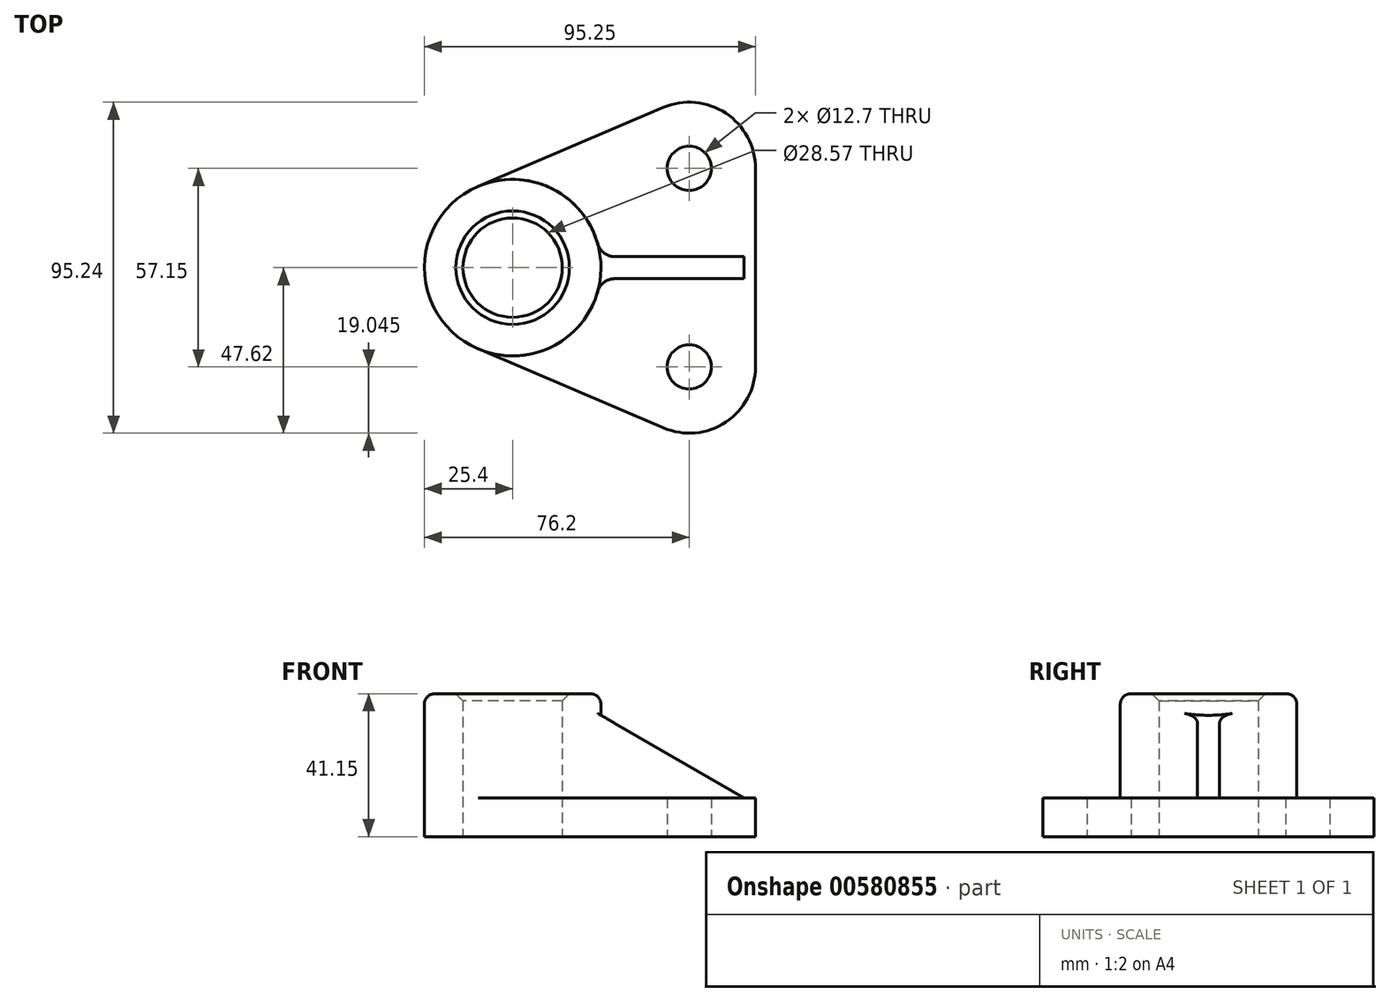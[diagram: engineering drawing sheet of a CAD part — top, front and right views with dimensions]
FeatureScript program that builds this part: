
annotation { "Feature Type Name" : "Feature", "Feature Type Description" : "" }
export const myFeature = defineFeature(function(context is Context, id is Id, definition is map)
    precondition{}
    {
        {
            var Q0;
            Q0=qCreatedBy(makeId("Top.planeOp"),FACE);
            var sketch = newSketch(context, id + "F0", { "sketchPlane" : qUnion([Q0])});
            skLineSegment(sketch, "E0", {"start": v(-101.4, 0) * mm, "end": v(116.06, 0) * mm, "construction": true});
            skCircle(sketch, "E1", {"center": v(0, 0) * mm, "radius": 14.29 * mm});
            skCircle(sketch, "E2", {"center": v(0, 0) * mm, "radius": 25.4 * mm});
            skCircle(sketch, "E3", {"center": v(50.8, -28.58) * mm, "radius": 6.35 * mm});
            skArc(sketch, "E4", {"start": v(43.33, -46.1) * mm, "mid": v(61.3, -44.47) * mm, "end": v(69.85, -28.57) * mm});
            skCircle(sketch, "E5", {"center": v(50.8, 28.58) * mm, "radius": 6.35 * mm});
            skArc(sketch, "E6", {"start": v(69.85, 28.58) * mm, "mid": v(61.3, 44.47) * mm, "end": v(43.33, 46.1) * mm});
            skLineSegment(sketch, "E7", {"start": v(69.85, 28.58) * mm, "end": v(69.85, -28.57) * mm});
            skLineSegment(sketch, "E8", {"start": v(-9.97, 23.36) * mm, "end": v(43.33, 46.1) * mm});
            skLineSegment(sketch, "E9", {"start": v(-9.97, -23.36) * mm, "end": v(43.33, -46.1) * mm});
            skSolve(sketch);
        }
        {
            var Q0;
            Q0=makeQuery(id+"F0.imprint","IMPRINT",FACE,{"disambiguationData":[TD([[makeQuery(id+"F0.imprint","IMPRINT",EDGE,{"derivedFrom":sQuery(id+"F0.wireOp",EDGE,"E1")}),-1.0]])]});
            extrude(context, id + "F1", {"entities" : qUnion([Q0]), "depth" : 41.15 * mm, "offsetDistance" : 25.4 * mm});
        }
        {
            var Q0;
            Q0=makeQuery(id+"F0.imprint","IMPRINT",FACE,{"disambiguationData":[TD([[makeQuery(id+"F0.imprint","IMPRINT",EDGE,{"derivedFrom":sQuery(id+"F0.wireOp",EDGE,"E3")}),-1.0]])]});
            extrude(context, id + "F2", {"entities" : qUnion([Q0]), "operationType" : NewBodyOperationType.ADD, "depth" : 11.18 * mm, "offsetDistance" : 25.4 * mm});
        }
        {
            var Q0;
            Q0=qCreatedBy(makeId("Front.planeOp"),FACE);
            var sketch = newSketch(context, id + "F3", { "sketchPlane" : qUnion([Q0])});
            skLineSegment(sketch, "E10", {"start": v(22.1, 36.84) * mm, "end": v(22.1, 11.18) * mm});
            skLineSegment(sketch, "E11", {"start": v(22.1, 11.18) * mm, "end": v(66.55, 11.18) * mm});
            skLineSegment(sketch, "E12", {"start": v(66.55, 11.18) * mm, "end": v(22.1, 36.84) * mm});
            skSolve(sketch);
        }
        {
            var Q0;
            Q0=makeQuery(id+"F3.imprint","IMPRINT",FACE,{"disambiguationData":[TD([[makeQuery(id+"F3.imprint","IMPRINT",EDGE,{"derivedFrom":sQuery(id+"F3.wireOp",EDGE,"E10")}),1.0]])]});
            extrude(context, id + "F4", {"entities" : qUnion([Q0]), "operationType" : NewBodyOperationType.ADD, "depth" : 6.35 * mm, "offsetDistance" : 25.4 * mm, "symmetric" : true});
        }
        {
            var Q0;
            Q0=makeQuery(id+"F1.opExtrude","CAP_EDGE",EDGE,{"disambiguationData":[OSD([sQuery(id+"F0.wireOp",EDGE,"E2")])],"isStart":false});
            fillet(context, id + "F5", {"entities" : qUnion([Q0]), "radius" : 3.05 * mm, "tangentPropagation" : true, "allowEdgeOverflow" : false});
        }
        {
            var Q0;
            Q0=makeQuery(id+"F4.opExtrude","CAP_EDGE",EDGE,{"disambiguationData":[OSD([sQuery(id+"F3.wireOp",EDGE,"E11")])],"isStart":true});
            var Q1;
            Q1=makeQuery(id+"F4.opExtrude","CAP_EDGE",EDGE,{"disambiguationData":[OSD([sQuery(id+"F3.wireOp",EDGE,"E11")])],"isStart":false});
            var Q2;
            {var subQ0=sQuery(id+"F0.wireOp",EDGE,"E2");var subQ1=sQuery(id+"F0.wireOp",EDGE,"E8");Q2=makeQuery(id+"F4.boolean.opBoolean","SPLIT",EDGE,{"disambiguationData":[TD([makeQuery(id+"F2.opExtrude","SWEPT_FACE",FACE,{"disambiguationData":[OSD([subQ1])]})])],"derivedFrom":makeQuery(id+"F2.opExtrude","CAP_EDGE",EDGE,{"disambiguationData":[OSD([subQ0])],"isStart":false})});}
            var Q3;
            {var subQ0=sQuery(id+"F0.wireOp",EDGE,"E2");var subQ1=sQuery(id+"F0.wireOp",EDGE,"E9");Q3=makeQuery(id+"F4.boolean.opBoolean","SPLIT",EDGE,{"disambiguationData":[TD([makeQuery(id+"F2.opExtrude","SWEPT_FACE",FACE,{"disambiguationData":[OSD([subQ1])]})])],"derivedFrom":makeQuery(id+"F2.opExtrude","CAP_EDGE",EDGE,{"disambiguationData":[OSD([subQ0])],"isStart":false})});}
            var Q4;
            Q4=makeQuery(id+"F4.boolean.opBoolean","INTERSECT",EDGE,{"derivedFrom":[makeQuery(id+"F1.opExtrude","SWEPT_FACE",FACE,{"disambiguationData":[OSD([sQuery(id+"F0.wireOp",EDGE,"E2")])]}),makeQuery(id+"F4.opExtrude","CAP_FACE",FACE,{"disambiguationData":[OSD([sQuery(id+"F3.wireOp",EDGE,"E10"),sQuery(id+"F3.wireOp",EDGE,"E11"),sQuery(id+"F3.wireOp",EDGE,"E12")])],"isStart":false})]});
            var Q5;
            Q5=makeQuery(id+"F4.boolean.opBoolean","INTERSECT",EDGE,{"derivedFrom":[makeQuery(id+"F1.opExtrude","SWEPT_FACE",FACE,{"disambiguationData":[OSD([sQuery(id+"F0.wireOp",EDGE,"E2")])]}),makeQuery(id+"F4.opExtrude","CAP_FACE",FACE,{"disambiguationData":[OSD([sQuery(id+"F3.wireOp",EDGE,"E10"),sQuery(id+"F3.wireOp",EDGE,"E11"),sQuery(id+"F3.wireOp",EDGE,"E12")])],"isStart":true})]});
            fillet(context, id + "F6", {"entities" : qUnion([Q0, Q1, Q2, Q3, Q4, Q5]), "radius" : 5.08 * mm, "tangentPropagation" : true, "allowEdgeOverflow" : false});
        }
        {
            var Q0;
            Q0=makeQuery(id+"F1.opExtrude","CAP_EDGE",EDGE,{"disambiguationData":[OSD([sQuery(id+"F0.wireOp",EDGE,"E1")])],"isStart":false});
            chamfer(context, id + "F7", {"entities" : qUnion([Q0]), "width" : 2.03 * mm, "tangentPropagation" : true});
        }
    });
